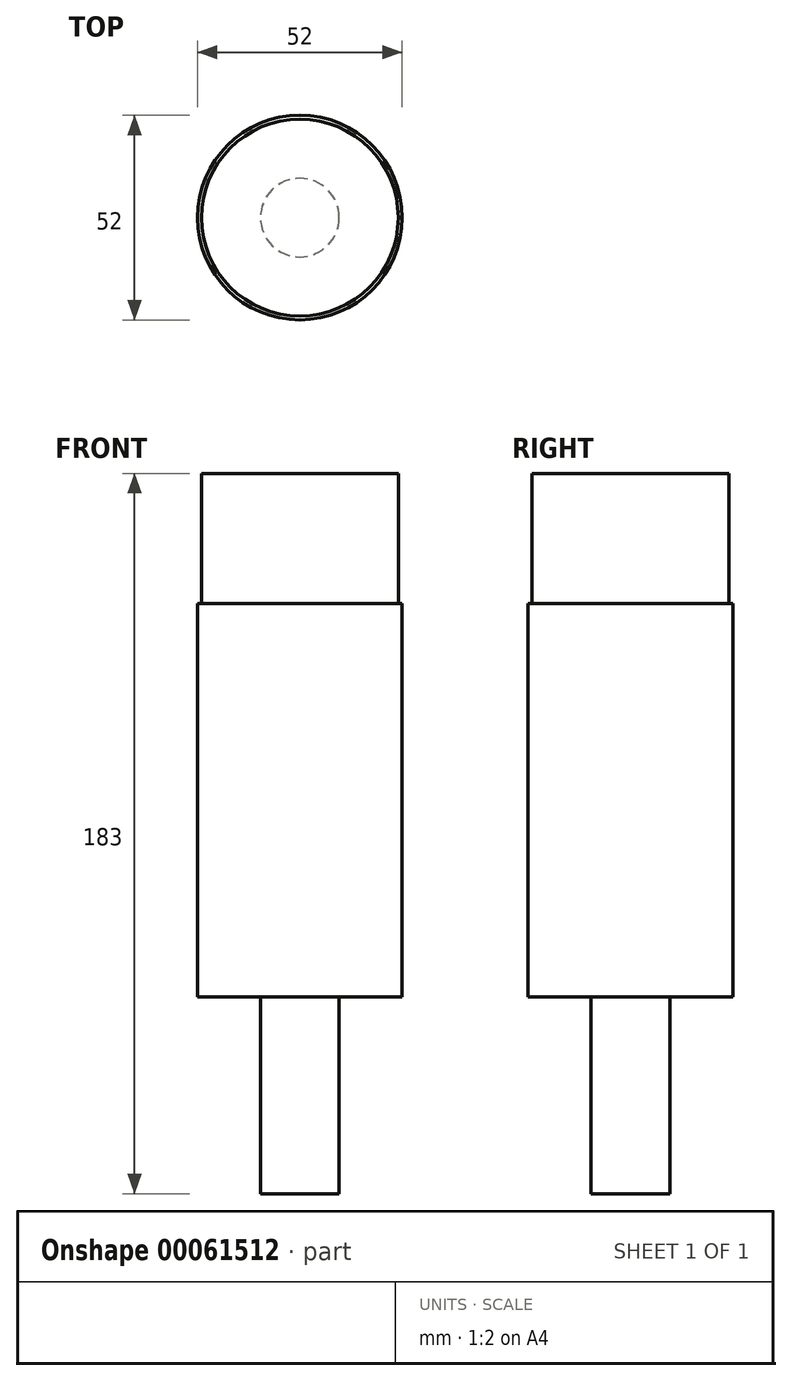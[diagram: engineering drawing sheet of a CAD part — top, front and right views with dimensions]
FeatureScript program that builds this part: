
annotation { "Feature Type Name" : "Feature", "Feature Type Description" : "" }
export const myFeature = defineFeature(function(context is Context, id is Id, definition is map)
    precondition{}
    {
        {
            var Q0;
            Q0=qCreatedBy(makeId("Top.planeOp"),FACE);
            var sketch = newSketch(context, id + "F0", { "sketchPlane" : qUnion([Q0])});
            skCircle(sketch, "E0", {"center": v(0, 0) * mm, "radius": 26 * mm});
            skSolve(sketch);
        }
        {
            var Q0;
            Q0=makeQuery(id+"F0.imprint","IMPRINT",FACE,{"disambiguationData":[TD([[makeQuery(id+"F0.imprint","IMPRINT",EDGE,{"derivedFrom":sQuery(id+"F0.wireOp",EDGE,"E0")}),1.0]])]});
            extrude(context, id + "F1", {"entities" : qUnion([Q0]), "depth" : 100 * mm, "symmetric" : true});
        }
        {
            var Q0;
            Q0=makeQuery(id+"F1.opExtrude","CAP_FACE",FACE,{"disambiguationData":[OSD([sQuery(id+"F0.wireOp",EDGE,"E0")])],"isStart":false});
            var sketch = newSketch(context, id + "F2", { "sketchPlane" : qUnion([Q0])});
            skCircle(sketch, "E1", {"center": v(0, 0) * mm, "radius": 25 * mm});
            skSolve(sketch);
        }
        {
            var Q0;
            Q0=makeQuery(id+"F2.imprint","IMPRINT",FACE,{"disambiguationData":[TD([[makeQuery(id+"F2.imprint","IMPRINT",EDGE,{"derivedFrom":sQuery(id+"F2.wireOp",EDGE,"E1")}),1.0]])]});
            extrude(context, id + "F3", {"entities" : qUnion([Q0]), "operationType" : NewBodyOperationType.ADD, "depth" : 33 * mm});
        }
        {
            var Q0;
            Q0=makeQuery(id+"F1.opExtrude","CAP_FACE",FACE,{"disambiguationData":[OSD([sQuery(id+"F0.wireOp",EDGE,"E0")])],"isStart":true});
            var sketch = newSketch(context, id + "F4", { "sketchPlane" : qUnion([Q0])});
            skCircle(sketch, "E2", {"center": v(0, 0) * mm, "radius": 10 * mm});
            skSolve(sketch);
        }
        {
            var Q0;
            Q0=makeQuery(id+"F4.imprint","IMPRINT",FACE,{"disambiguationData":[TD([[makeQuery(id+"F4.imprint","IMPRINT",EDGE,{"derivedFrom":sQuery(id+"F4.wireOp",EDGE,"E2")}),1.0]])]});
            extrude(context, id + "F5", {"entities" : qUnion([Q0]), "operationType" : NewBodyOperationType.ADD, "depth" : 50 * mm});
        }
    });
